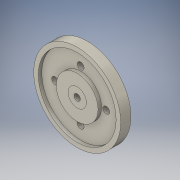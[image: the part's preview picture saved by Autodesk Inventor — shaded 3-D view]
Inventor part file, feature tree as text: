
AUTODESK INVENTOR PART (.ipt)
format: ipt  version: 2016 (Build 200138000, 138)  size: 187,904 bytes
history: native  units: in
note: dims shown in document units (in); Inventor stores cm internally (conversion verified against a paired STEP export)
features: extrude x7, sketch x7, plane x1
ambient origin geometry x8: Origin, YZ Plane, XZ Plane, XY Plane, X Axis, Y Axis, Z Axis, Center Point
bodies: Solid1 (feature_tree)
feature tree (15):
  extrude  "Extrusion1"  Depth=0.2in TaperAngle=0.0deg
  extrude  "Extrusion2"  Depth=1.52in
  extrude  "Extrusion3"  Depth=0.36in
  extrude  "Extrusion5"  Depth=0.5in TaperAngle=0.0deg
  extrude  "Extrusion6"  Depth=0.18in TaperAngle=0.0deg
  extrude  "Extrusion8"  Depth=0.133in
  plane  "Work Plane1"
  extrude  "Extrusion9"  Depth=0.5in
  sketch  "Sketch1"  dims[d0=1.7in d1=0.2in d2=0.0in]
  sketch  "Sketch2"  dims[d3=0.816in d4=1.52in]
  sketch  "Sketch3"  dims[d5=0.068in d6=0.0in d7=0.36in]
  sketch  "Sketch5"  dims[d8=0.0001in d9=0.5in d10=0.0in d11=0.0in d17=0.45in d18=0.0in]
  sketch  "Sketch6"  dims[d19=0.125in d20=0.18in d21=0.0in]
  sketch  "Sketch8"  dims[d25=0.133in d26=0.133in]
  sketch  "Sketch9"  dims[d29=0.133in d30=0.133in d33=1.0in d34=0.0in d35=0.1in d36=1.0in d37=0.0in d38=0.5in d39=0.5in d40=0.5in d41=0.5in]
